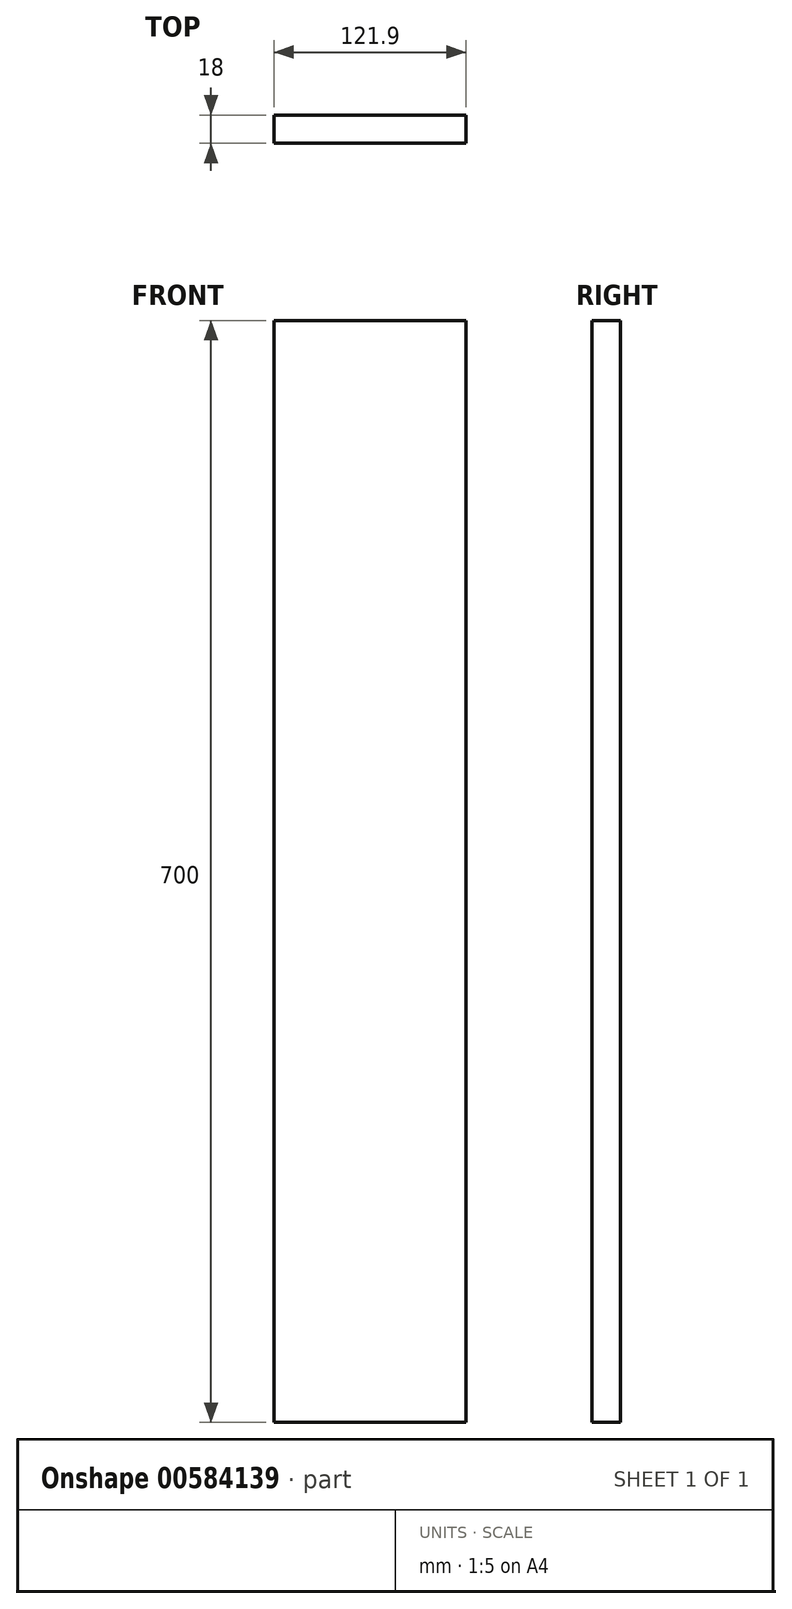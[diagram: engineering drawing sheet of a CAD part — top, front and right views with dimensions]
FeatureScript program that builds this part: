
annotation { "Feature Type Name" : "Feature", "Feature Type Description" : "" }
export const myFeature = defineFeature(function(context is Context, id is Id, definition is map)
    precondition{}
    {
        {
            var Q0;
            Q0=qCreatedBy(makeId("Front.planeOp"),FACE);
            var sketch = newSketch(context, id + "F0", { "sketchPlane" : qUnion([Q0])});
            skLineSegment(sketch, "E0", {"start": v(0, 0) * mm, "end": v(0, -700) * mm});
            skLineSegment(sketch, "E1", {"start": v(0, -700) * mm, "end": v(121.9, -700) * mm});
            skLineSegment(sketch, "E2", {"start": v(121.9, -700) * mm, "end": v(121.9, 0) * mm});
            skLineSegment(sketch, "E3", {"start": v(121.9, 0) * mm, "end": v(0, 0) * mm});
            skSolve(sketch);
        }
        {
            var Q0;
            Q0 = qSketchRegion(id + "F0", true);
            extrude(context, id + "F1", {"entities" : qUnion([Q0]), "depth" : 18 * mm, "offsetDistance" : 25 * mm});
        }
    });
